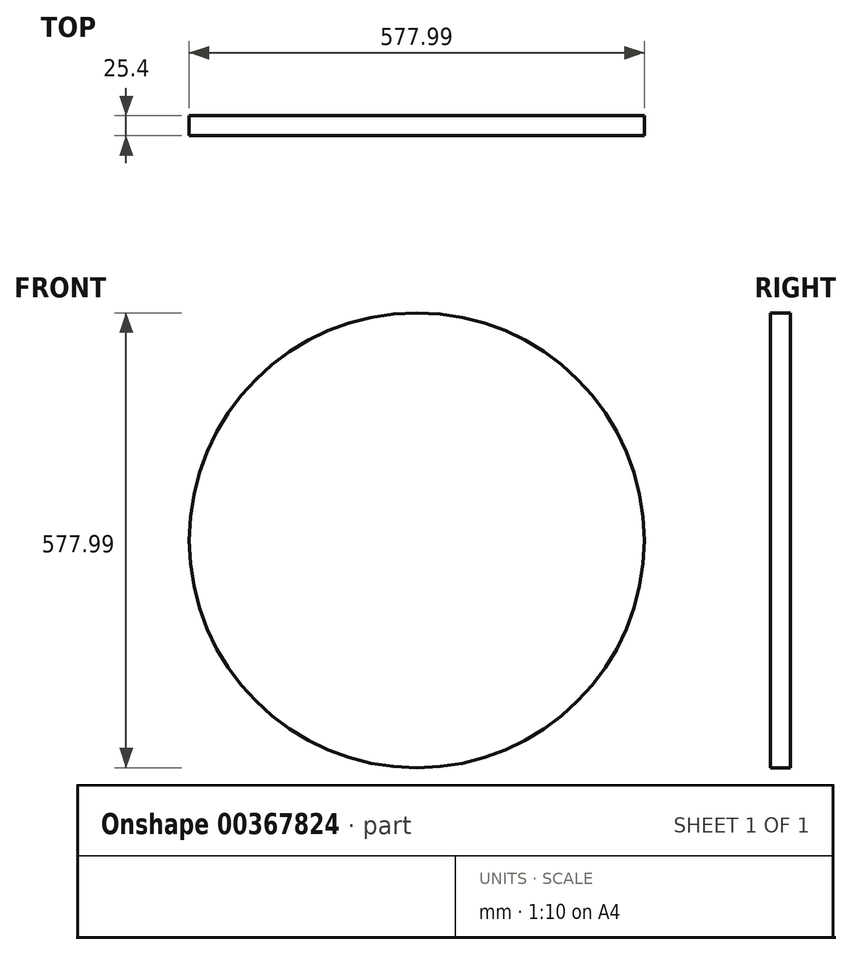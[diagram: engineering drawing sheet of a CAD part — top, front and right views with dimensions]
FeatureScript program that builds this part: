
annotation { "Feature Type Name" : "Feature", "Feature Type Description" : "" }
export const myFeature = defineFeature(function(context is Context, id is Id, definition is map)
    precondition{}
    {
        {
            var Q0;
            Q0=qCreatedBy(makeId("Front.planeOp"),FACE);
            var sketch = newSketch(context, id + "F0", { "sketchPlane" : qUnion([Q0])});
            skCircle(sketch, "E0", {"center": v(-288.55, -15.9) * mm, "radius": 289 * mm});
            skSolve(sketch);
        }
        {
            var Q0;
            Q0 = qSketchRegion(id + "F0", true);
            extrude(context, id + "F1", {"entities" : qUnion([Q0]), "depth" : 25.4 * mm});
        }
    });
